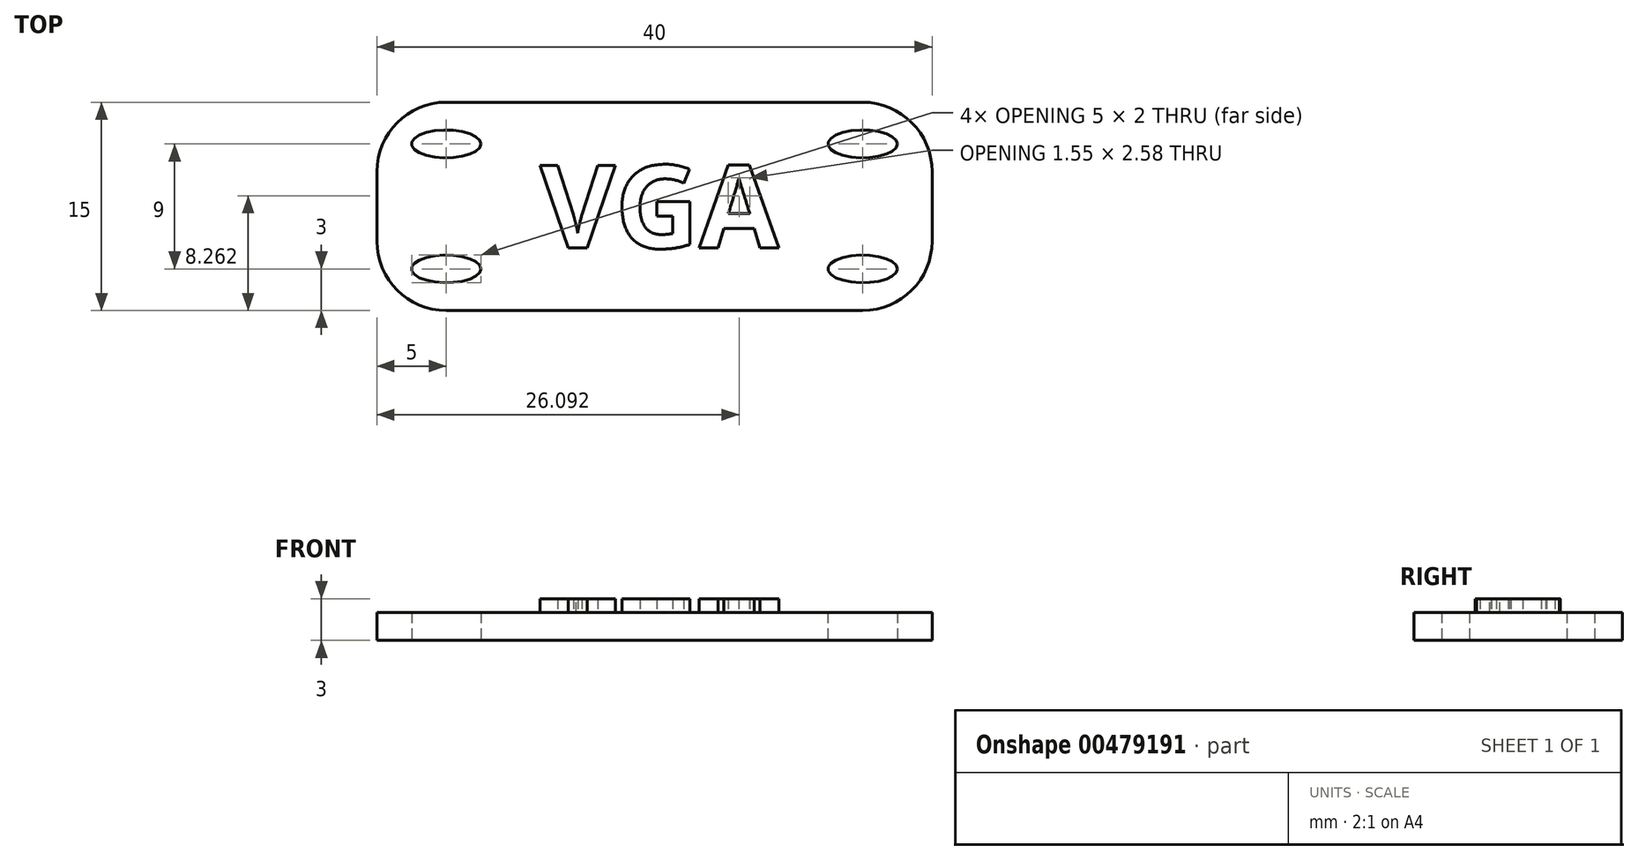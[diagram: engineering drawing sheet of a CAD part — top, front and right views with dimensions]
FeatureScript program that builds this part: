
annotation { "Feature Type Name" : "Feature", "Feature Type Description" : "" }
export const myFeature = defineFeature(function(context is Context, id is Id, definition is map)
    precondition{}
    {
        {
            var Q0;
            Q0=qCreatedBy(makeId("Top.planeOp"),FACE);
            var sketch = newSketch(context, id + "F0", { "sketchPlane" : qUnion([Q0])});
            skLineSegment(sketch, "E0.bottom", {"start": v(20, -7.5) * mm, "end": v(-20, -7.5) * mm});
            skLineSegment(sketch, "E0.top", {"start": v(20, 7.5) * mm, "end": v(-20, 7.5) * mm});
            skLineSegment(sketch, "E0.left", {"start": v(20, -7.5) * mm, "end": v(20, 7.5) * mm});
            skLineSegment(sketch, "E0.right", {"start": v(-20, -7.5) * mm, "end": v(-20, 7.5) * mm});
            skPoint(sketch, "E0.middle", {"position": v(0, 0) * mm});
            skLineSegment(sketch, "E1", {"start": v(-20, -4.5) * mm, "end": v(20, -4.5) * mm, "construction": true});
            skPoint(sketch, "E2", {"position": v(-15, -4.5) * mm});
            skEllipse(sketch, "E3", {"center": v(-15, -4.5) * mm, "majorRadius": 2.5 * mm, "minorRadius": 1 * mm, "majorAxis": v(1, 0)});
            skEllipse(sketch, "E4.1.0.0", {"center": v(15, -4.5) * mm, "majorRadius": 2.5 * mm, "minorRadius": 1 * mm, "majorAxis": v(1, 0)});
            skLineSegment(sketch, "E4.direction1", {"start": v(-15, -4.5) * mm, "end": v(15, -4.5) * mm, "construction": true});
            skLineSegment(sketch, "E5", {"start": v(20, 0) * mm, "end": v(-20, 0) * mm, "construction": true});
            skEllipse(sketch, "E6.MirrorC", {"center": v(15, 4.5) * mm, "majorRadius": 2.5 * mm, "minorRadius": 1 * mm, "majorAxis": v(1, 0)});
            skEllipse(sketch, "E7.MirrorC", {"center": v(-15, 4.5) * mm, "majorRadius": 2.5 * mm, "minorRadius": 1 * mm, "majorAxis": v(1, 0)});
            skSolve(sketch);
        }
        {
            var Q0;
            Q0=makeQuery(id+"F0.imprint","IMPRINT",FACE,{"disambiguationData":[TD([[makeQuery(id+"F0.imprint","IMPRINT",EDGE,{"derivedFrom":sQuery(id+"F0.wireOp",EDGE,"E0.bottom")}),-1.0]])]});
            extrude(context, id + "F1", {"entities" : qUnion([Q0]), "depth" : 2 * mm});
        }
        {
            var Q0;
            Q0=makeQuery(id+"F1.opExtrude","CAP_FACE",FACE,{"disambiguationData":[OSD([sQuery(id+"F0.wireOp",EDGE,"E0.bottom"),sQuery(id+"F0.wireOp",EDGE,"E0.top"),sQuery(id+"F0.wireOp",EDGE,"E0.left"),sQuery(id+"F0.wireOp",EDGE,"E0.right"),sQuery(id+"F0.wireOp",EDGE,"E3"),sQuery(id+"F0.wireOp",EDGE,"E4.1.0.0"),sQuery(id+"F0.wireOp",EDGE,"E6.MirrorC"),sQuery(id+"F0.wireOp",EDGE,"E7.MirrorC")])],"isStart":false});
            var sketch = newSketch(context, id + "F2", { "sketchPlane" : qUnion([Q0])});
            skText(sketch, "E8", { "text": "VGA", "fontName": "OpenSans-Bold.ttf"});
            const initialGuessF2  = {"E8": [-0.00824, -0.003, 1, 0, 0.006]};
            skSetInitialGuess(sketch, initialGuessF2);
            skSolve(sketch);
        }
        {
            var Q0;
            Q0=qSketchRegion(id+"F2",true);
            extrude(context, id + "F3", {"entities" : qUnion([Q0]), "depth" : 1 * mm});
        }
        {
            var Q0;
            Q0=makeQuery(id+"F1.opExtrude","SWEPT_EDGE",EDGE,{"disambiguationData":[OSD([sQuery(id+"F0.wireOp",EDGE,"E0.bottom"),sQuery(id+"F0.wireOp",EDGE,"E0.right")])]});
            var Q1;
            Q1=makeQuery(id+"F1.opExtrude","SWEPT_EDGE",EDGE,{"disambiguationData":[OSD([sQuery(id+"F0.wireOp",EDGE,"E0.bottom"),sQuery(id+"F0.wireOp",EDGE,"E0.left")])]});
            var Q2;
            Q2=makeQuery(id+"F1.opExtrude","SWEPT_EDGE",EDGE,{"disambiguationData":[OSD([sQuery(id+"F0.wireOp",EDGE,"E0.top"),sQuery(id+"F0.wireOp",EDGE,"E0.left")])]});
            var Q3;
            Q3=makeQuery(id+"F1.opExtrude","SWEPT_EDGE",EDGE,{"disambiguationData":[OSD([sQuery(id+"F0.wireOp",EDGE,"E0.top"),sQuery(id+"F0.wireOp",EDGE,"E0.right")])]});
            fillet(context, id + "F4", {"entities" : qUnion([Q0, Q1, Q2, Q3]), "radius" : 5 * mm, "tangentPropagation" : true, "allowEdgeOverflow" : false});
        }
    });
